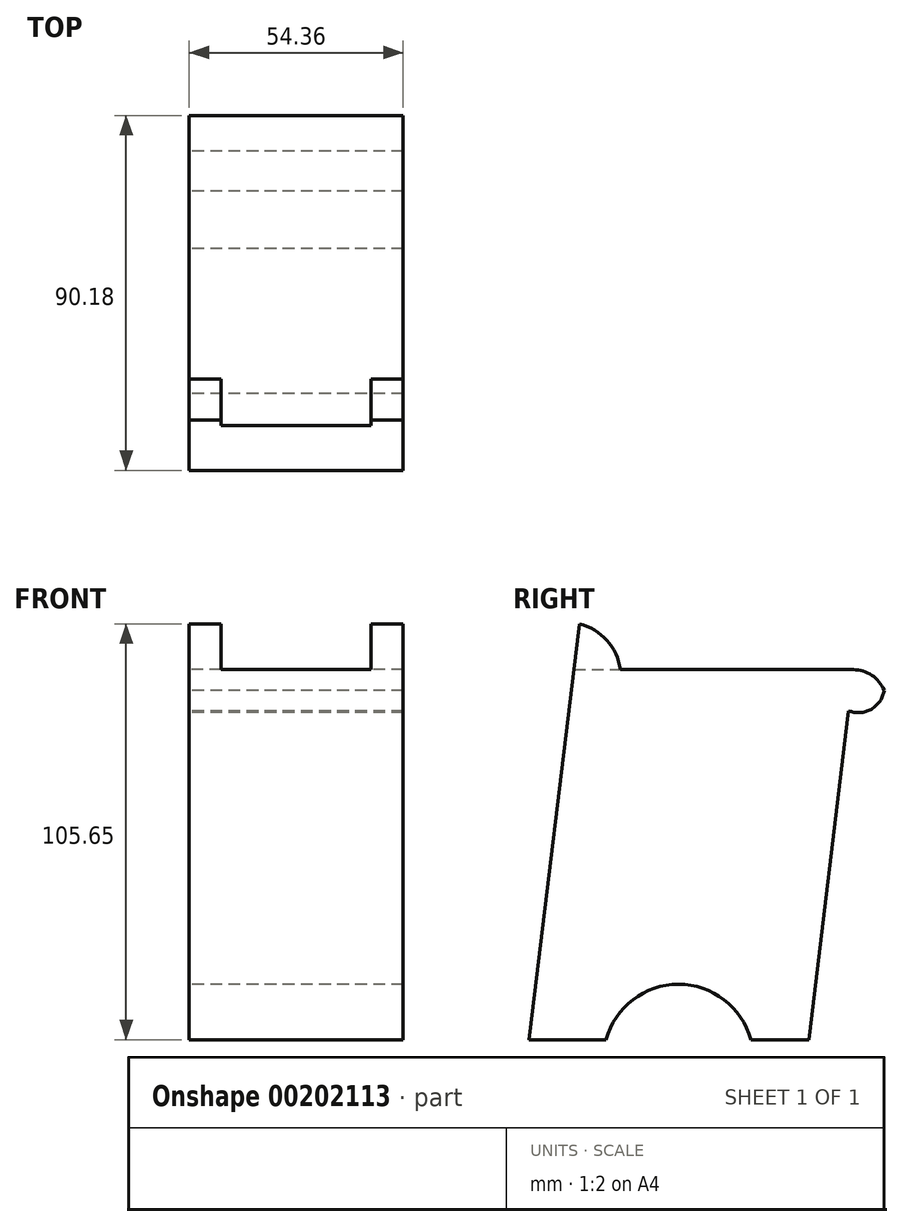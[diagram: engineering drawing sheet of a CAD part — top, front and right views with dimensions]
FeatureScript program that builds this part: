
annotation { "Feature Type Name" : "Feature", "Feature Type Description" : "" }
export const myFeature = defineFeature(function(context is Context, id is Id, definition is map)
    precondition{}
    {
        {
            var Q0;
            Q0=qCreatedBy(makeId("Right.planeOp"),FACE);
            var sketch = newSketch(context, id + "F0", { "sketchPlane" : qUnion([Q0])});
            skArc(sketch, "E0", {"start": v(21.37, 0) * mm, "mid": v(3, 14.08) * mm, "end": v(-15.38, 0) * mm});
            skLineSegment(sketch, "E1", {"start": v(-15.38, 0) * mm, "end": v(-34.92, 0) * mm});
            skLineSegment(sketch, "E2", {"start": v(-34.92, 0) * mm, "end": v(-23.6, 94) * mm});
            skLineSegment(sketch, "E3", {"start": v(21.37, 0) * mm, "end": v(36.1, 0) * mm});
            skLineSegment(sketch, "E4", {"start": v(36.1, 0) * mm, "end": v(47.42, 94) * mm});
            skLineSegment(sketch, "E5", {"start": v(-23.6, 94) * mm, "end": v(47.42, 94) * mm});
            skLineSegment(sketch, "E6", {"start": v(-23.6, 94) * mm, "end": v(-22.2, 105.65) * mm});
            skArc(sketch, "E7", {"start": v(-11.77, 94) * mm, "mid": v(-15.18, 101.44) * mm, "end": v(-22.2, 105.65) * mm});
            skArc(sketch, "E8", {"start": v(55.26, 88.76) * mm, "mid": v(52.13, 92.57) * mm, "end": v(47.42, 94) * mm});
            skArc(sketch, "E9", {"start": v(46.16, 83.57) * mm, "mid": v(51.97, 83.95) * mm, "end": v(55.26, 88.76) * mm});
            skSolve(sketch);
        }
        {
            var Q0;
            Q0=makeQuery(id+"F0.imprint","IMPRINT",FACE,{"disambiguationData":[TD([[makeQuery(id+"F0.imprint","IMPRINT",EDGE,{"derivedFrom":sQuery(id+"F0.wireOp",EDGE,"E0")}),-1.0]])]});
            var Q1;
            {var subQ0=sQuery(id+"F0.wireOp",EDGE,"E8");Q1=makeQuery(id+"F0.imprint","IMPRINT",FACE,{"disambiguationData":[TD([[makeQuery(id+"F0.imprint","IMPRINT",EDGE,{"derivedFrom":subQ0}),1.0]])]});}
            extrude(context, id + "F1", {"entities" : qUnion([Q0, Q1]), "depth" : 54.36 * mm});
        }
        {
            var Q0;
            {var subQ0=sQuery(id+"F0.wireOp",EDGE,"E6");Q0=makeQuery(id+"F0.imprint","IMPRINT",FACE,{"disambiguationData":[TD([[makeQuery(id+"F0.imprint","IMPRINT",EDGE,{"derivedFrom":subQ0}),-1.0]])]});}
            extrude(context, id + "F2", {"entities" : qUnion([Q0]), "operationType" : NewBodyOperationType.ADD, "depth" : 8.13 * mm});
        }
        {
            var Q0;
            Q0=makeQuery(id+"F2.opExtrude","CAP_FACE",FACE,{"disambiguationData":[OSD([sQuery(id+"F0.wireOp",EDGE,"E5"),sQuery(id+"F0.wireOp",EDGE,"E6"),sQuery(id+"F0.wireOp",EDGE,"E7")])],"isStart":false});
            extrude(context, id + "F3", {"entities" : qUnion([Q0]), "operationType" : NewBodyOperationType.ADD, "depth" : 46.23 * mm, "hasSecondDirection" : true, "secondDirectionOppositeDirection" : false, "secondDirectionDepth" : 38.1 * mm});
        }
    });
